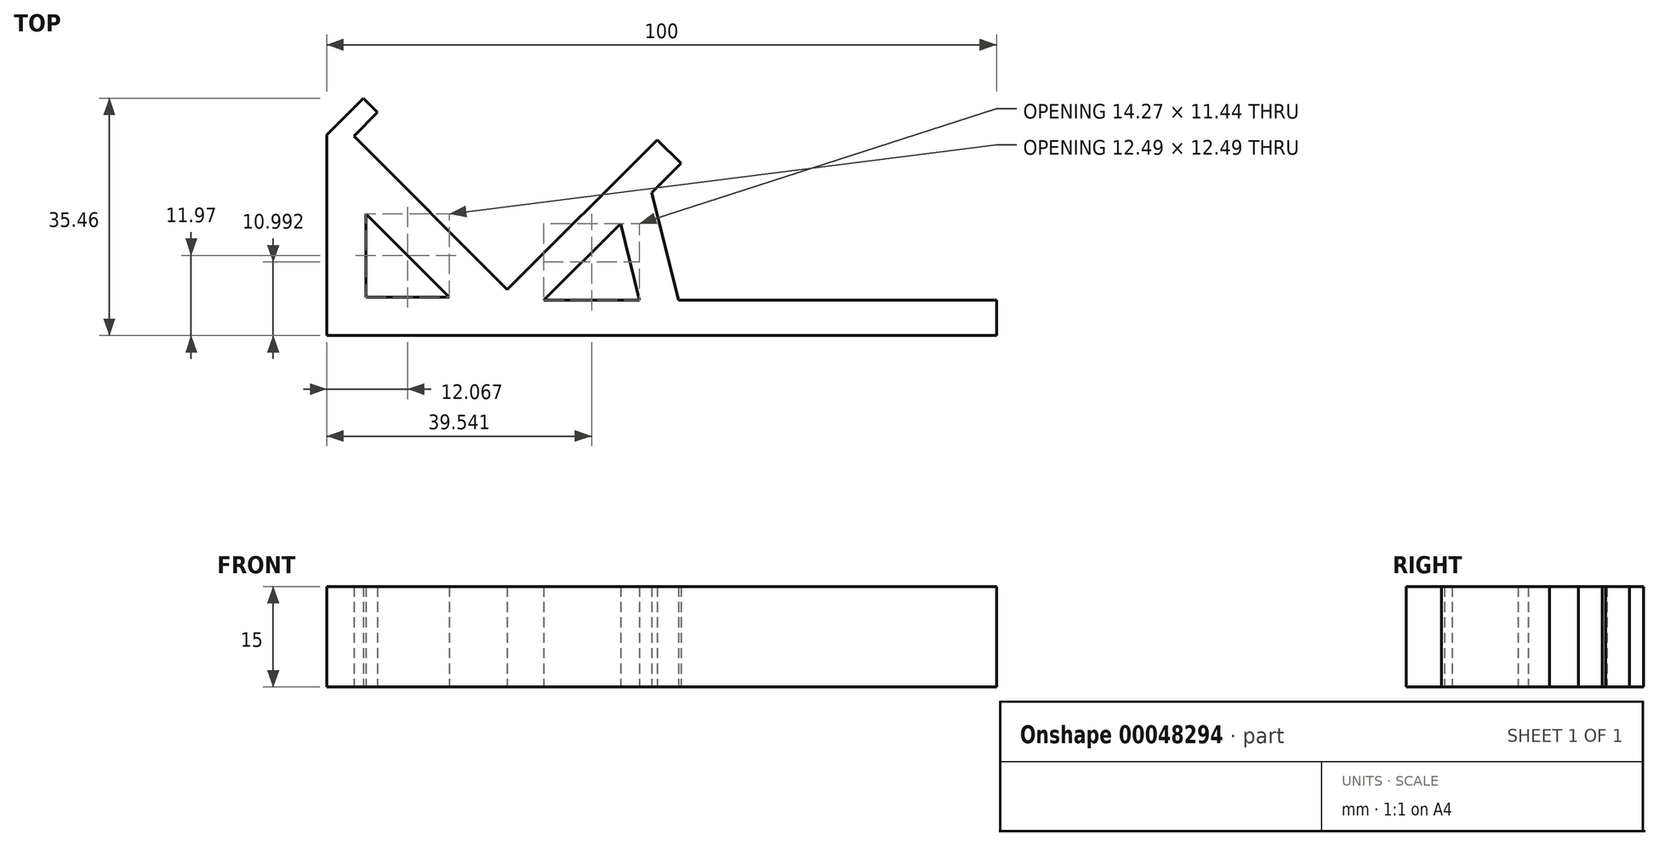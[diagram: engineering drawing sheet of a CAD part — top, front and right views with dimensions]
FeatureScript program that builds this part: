
annotation { "Feature Type Name" : "Feature", "Feature Type Description" : "" }
export const myFeature = defineFeature(function(context is Context, id is Id, definition is map)
    precondition{}
    {
        {
            var Q0;
            Q0=qCreatedBy(makeId("Top.planeOp"),FACE);
            var sketch = newSketch(context, id + "F0", { "sketchPlane" : qUnion([Q0])});
            skLineSegment(sketch, "E0", {"start": v(0, 0) * mm, "end": v(100, 0) * mm});
            skLineSegment(sketch, "E1", {"start": v(100, 0) * mm, "end": v(100, 5.27) * mm});
            skLineSegment(sketch, "E2", {"start": v(100, 5.27) * mm, "end": v(52.5, 5.27) * mm});
            skLineSegment(sketch, "E3", {"start": v(48.51, 21.38) * mm, "end": v(52.86, 25.73) * mm});
            skLineSegment(sketch, "E4", {"start": v(52.86, 25.73) * mm, "end": v(49.33, 29.26) * mm});
            skLineSegment(sketch, "E5", {"start": v(49.33, 29.26) * mm, "end": v(26.95, 6.89) * mm});
            skLineSegment(sketch, "E6", {"start": v(26.95, 6.89) * mm, "end": v(4.04, 29.8) * mm});
            skLineSegment(sketch, "E7", {"start": v(4.04, 29.8) * mm, "end": v(7.58, 33.33) * mm});
            skLineSegment(sketch, "E8", {"start": v(7.58, 33.33) * mm, "end": v(5.46, 35.46) * mm});
            skLineSegment(sketch, "E9", {"start": v(5.46, 35.46) * mm, "end": v(0, 30) * mm});
            skLineSegment(sketch, "E10", {"start": v(0, 30) * mm, "end": v(0, 0) * mm});
            skPoint(sketch, "E11.visualSharp", {"position": v(32.4, 5.27) * mm});
            skLineSegment(sketch, "E12", {"start": v(48.51, 21.38) * mm, "end": v(52.5, 5.27) * mm});
            skLineSegment(sketch, "E13", {"start": v(5.82, 18.22) * mm, "end": v(5.82, 5.72) * mm});
            skLineSegment(sketch, "E14", {"start": v(32.4, 5.27) * mm, "end": v(43.85, 16.71) * mm});
            skLineSegment(sketch, "E15", {"start": v(43.85, 16.71) * mm, "end": v(46.68, 5.27) * mm});
            skLineSegment(sketch, "E16", {"start": v(46.68, 5.27) * mm, "end": v(32.4, 5.27) * mm});
            skLineSegment(sketch, "E17", {"start": v(5.82, 18.22) * mm, "end": v(18.31, 5.72) * mm});
            skLineSegment(sketch, "E18", {"start": v(18.31, 5.72) * mm, "end": v(5.82, 5.72) * mm});
            skSolve(sketch);
        }
        {
            var Q0;
            Q0=makeQuery(id+"F0.imprint","IMPRINT",FACE,{"disambiguationData":[TD([[makeQuery(id+"F0.imprint","IMPRINT",EDGE,{"derivedFrom":sQuery(id+"F0.wireOp",EDGE,"E0")}),1.0]])]});
            extrude(context, id + "F1", {"entities" : qUnion([Q0]), "depth" : 15 * mm});
        }
    });
